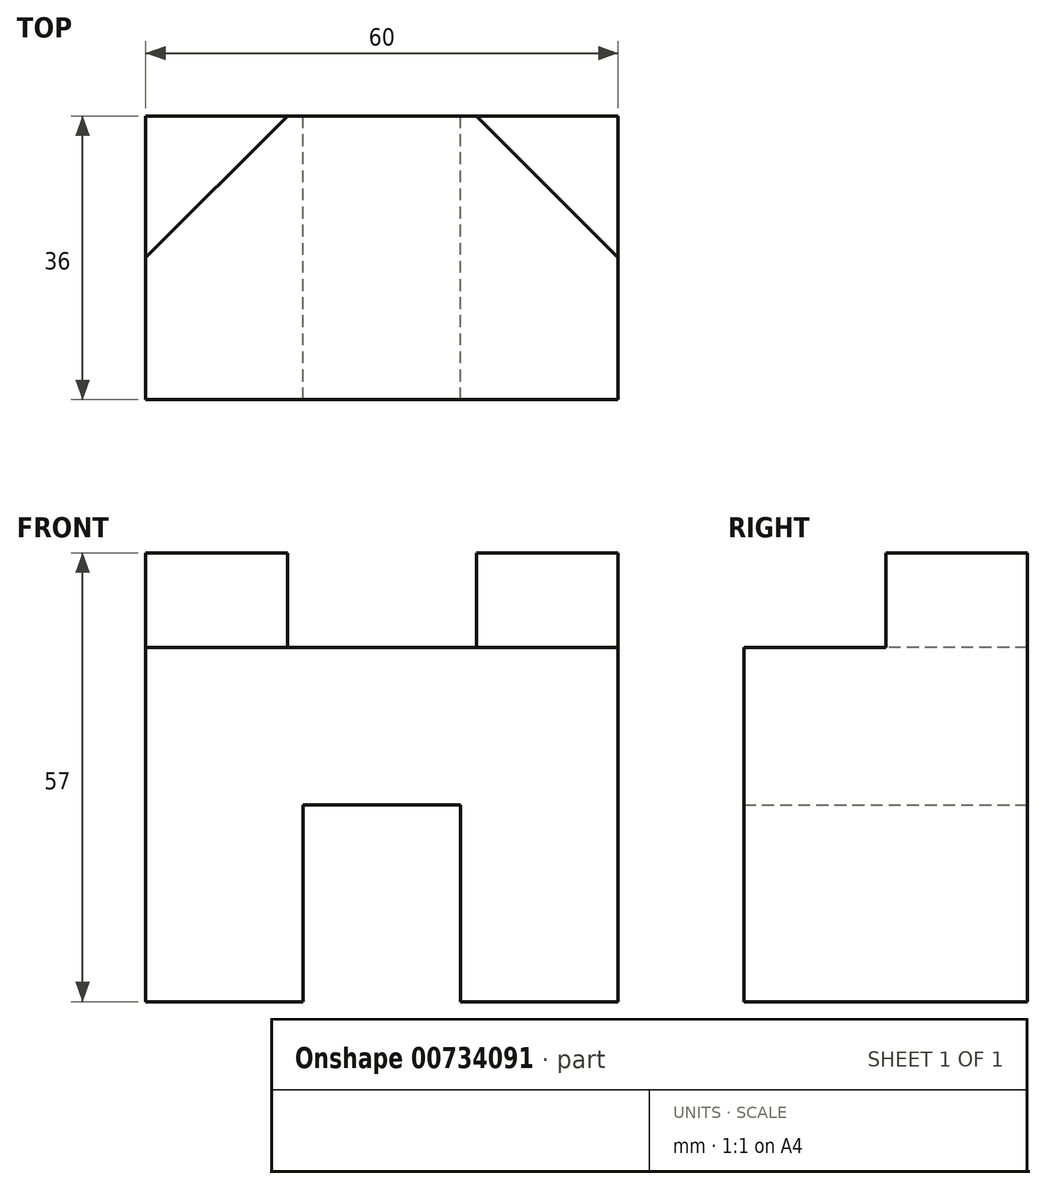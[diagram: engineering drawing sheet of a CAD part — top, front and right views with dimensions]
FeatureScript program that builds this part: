
annotation { "Feature Type Name" : "Feature", "Feature Type Description" : "" }
export const myFeature = defineFeature(function(context is Context, id is Id, definition is map)
    precondition{}
    {
        {
            var Q0;
            Q0=qCreatedBy(makeId("Front.planeOp"),FACE);
            var sketch = newSketch(context, id + "F0", { "sketchPlane" : qUnion([Q0])});
            skLineSegment(sketch, "E0.bottom", {"start": v(-30, 22.5) * mm, "end": v(30, 22.5) * mm});
            skLineSegment(sketch, "E0.top", {"start": v(-30, -22.5) * mm, "end": v(-10, -22.5) * mm});
            skLineSegment(sketch, "E0.left", {"start": v(-30, 22.5) * mm, "end": v(-30, -22.5) * mm});
            skLineSegment(sketch, "E0.right", {"start": v(30, 22.5) * mm, "end": v(30, -22.5) * mm});
            skPoint(sketch, "E0.middle", {"position": v(0, 0) * mm});
            skLineSegment(sketch, "E1.bottom", {"start": v(-10, 2.5) * mm, "end": v(10, 2.5) * mm});
            skLineSegment(sketch, "E1.left", {"start": v(-10, 2.5) * mm, "end": v(-10, -22.5) * mm});
            skLineSegment(sketch, "E1.right", {"start": v(10, 2.5) * mm, "end": v(10, -22.5) * mm});
            skPoint(sketch, "E1.middle", {"position": v(0, -22.5) * mm});
            skLineSegment(sketch, "E2.trimOffspring", {"start": v(10, -22.5) * mm, "end": v(30, -22.5) * mm});
            skPoint(sketch, "E3.orphan", {"position": v(-10, -47.5) * mm});
            skPoint(sketch, "E4.orphan", {"position": v(10, -47.5) * mm});
            skSolve(sketch);
        }
        {
            var Q0;
            Q0 = qSketchRegion(id + "F0", true);
            extrude(context, id + "F1", {"entities" : qUnion([Q0]), "depth" : 36 * mm, "offsetDistance" : 25 * mm});
        }
        {
            var Q0;
            Q0=makeQuery(id+"F1.opExtrude","SWEPT_FACE",FACE,{"disambiguationData":[OSD([sQuery(id+"F0.wireOp",EDGE,"E0.bottom")])]});
            var sketch = newSketch(context, id + "F2", { "sketchPlane" : qUnion([Q0])});
            skLineSegment(sketch, "E5.bottom", {"start": v(30, 0) * mm, "end": v(12, 0) * mm});
            skLineSegment(sketch, "E5.left", {"start": v(30, 0) * mm, "end": v(30, -18) * mm});
            skLineSegment(sketch, "E6.bottom", {"start": v(-30, 0) * mm, "end": v(-12, 0) * mm});
            skLineSegment(sketch, "E6.left", {"start": v(-30, 0) * mm, "end": v(-30, -18) * mm});
            skLineSegment(sketch, "E7", {"start": v(-12, 0) * mm, "end": v(-30, -18) * mm});
            skLineSegment(sketch, "E8", {"start": v(12, 0) * mm, "end": v(30, -18) * mm});
            skPoint(sketch, "E5.right.end.orphan", {"position": v(12, -18) * mm});
            skPoint(sketch, "E6.top.end.orphan", {"position": v(-12, -18) * mm});
            skSolve(sketch);
        }
        {
            var Q0;
            Q0=makeQuery(id+"F2.imprint","IMPRINT",FACE,{"disambiguationData":[TD([[makeQuery(id+"F2.imprint","IMPRINT",EDGE,{"derivedFrom":sQuery(id+"F2.wireOp",EDGE,"E5.bottom")}),-1.0]])]});
            var Q1;
            Q1=makeQuery(id+"F2.imprint","IMPRINT",FACE,{"disambiguationData":[TD([[makeQuery(id+"F2.imprint","IMPRINT",EDGE,{"derivedFrom":sQuery(id+"F2.wireOp",EDGE,"E6.bottom")}),-1.0]])]});
            extrude(context, id + "F3", {"entities" : qUnion([Q0, Q1]), "operationType" : NewBodyOperationType.ADD, "depth" : 12 * mm, "offsetDistance" : 25 * mm});
        }
    });
